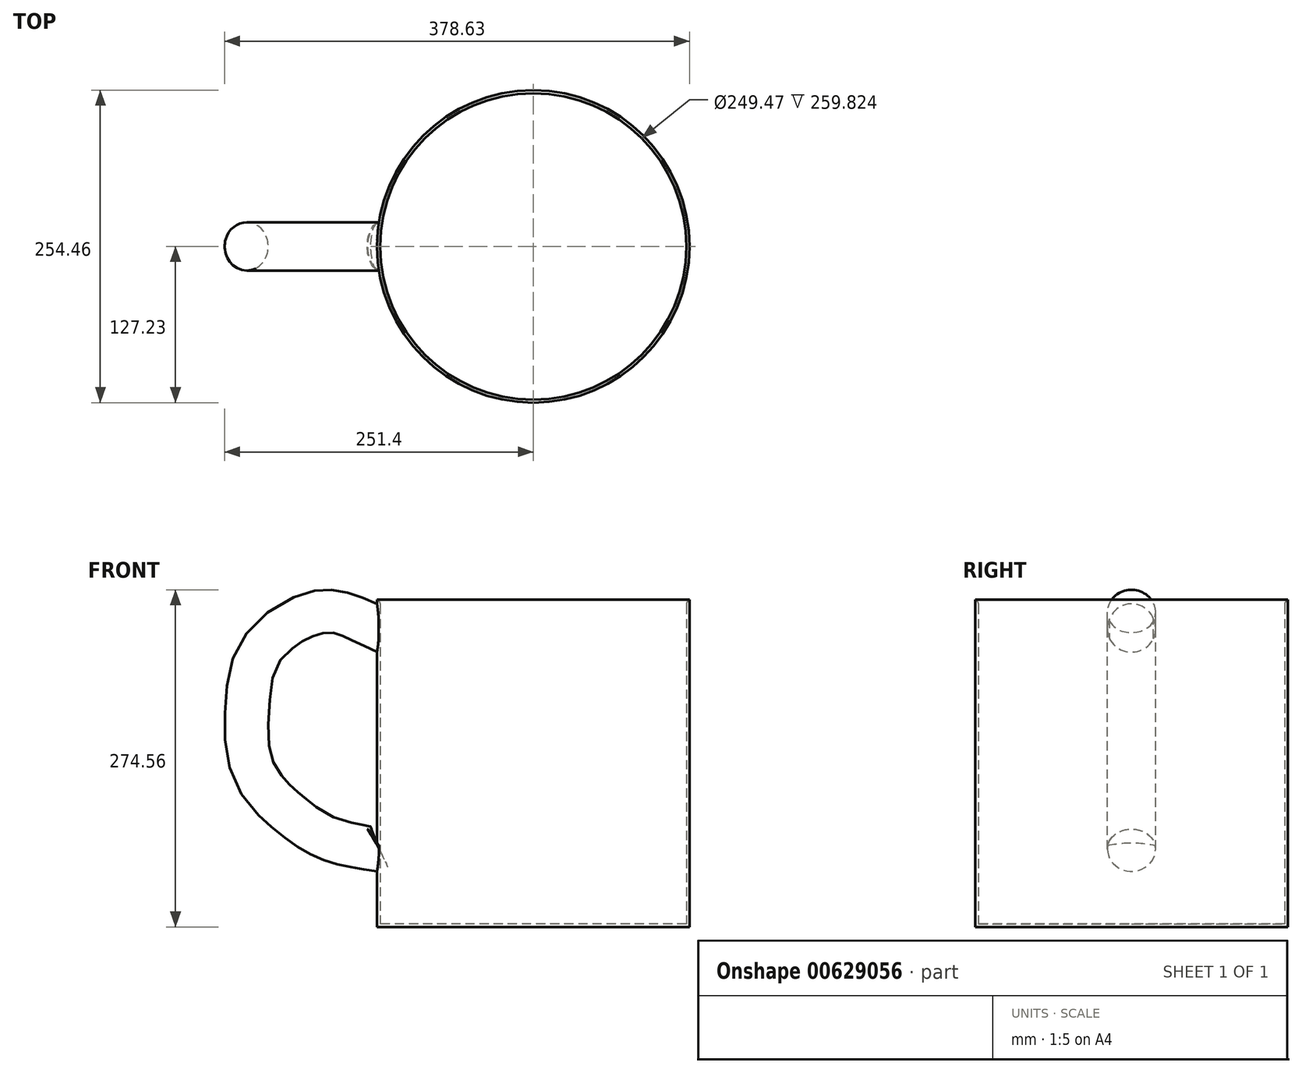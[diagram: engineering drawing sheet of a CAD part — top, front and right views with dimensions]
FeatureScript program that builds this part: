
annotation { "Feature Type Name" : "Feature", "Feature Type Description" : "" }
export const myFeature = defineFeature(function(context is Context, id is Id, definition is map)
    precondition{}
    {
        {
            var Q0;
            Q0=qCreatedBy(makeId("Top.planeOp"),FACE);
            var sketch = newSketch(context, id + "F0", { "sketchPlane" : qUnion([Q0])});
            skCircle(sketch, "E0", {"center": v(0, 0) * mm, "radius": 127.23 * mm});
            skSolve(sketch);
        }
        {
            var Q0;
            Q0 = qSketchRegion(id + "F0", true);
            extrude(context, id + "F1", {"entities" : qUnion([Q0]), "depth" : 266.7 * mm, "offsetDistance" : 25.4 * mm});
        }
        {
            var Q0;
            Q0=qCreatedBy(makeId("Front.planeOp"),FACE);
            var sketch = newSketch(context, id + "F2", { "sketchPlane" : qUnion([Q0])});
            skFitSpline(sketch, "E1", {"points": [v(-125.96, 244.42) * mm, v(-174.92, 257.06) * mm, v(-221.52, 227.05) * mm, v(-234.15, 180.45) * mm, v(-227.84, 125.17) * mm, v(-193.09, 86.48) * mm, v(-159.13, 68.31) * mm, v(-125.96, 62) * mm, v(-122.94, 62.13) * mm], "startDerivative": vector(-388.45, 179.87) * mm, "endDerivative": vector(138.8, 21.72) * mm});
            skSolve(sketch);
        }
        {
            var Q0;
            Q0=qCreatedBy(makeId("Right.planeOp"),FACE);
            cPlane(context, id + "F3", {"entities" : qUnion([Q0]), "cplaneType" : CPlaneType.OFFSET, "offset" : 128.27 * mm, "oppositeDirection" : true, "width" : 152.4 * mm, "height" : 152.4 * mm});
        }
        {
            var Q0;
            Q0=qCreatedBy(id+"F3.planeOp",FACE);
            var sketch = newSketch(context, id + "F4", { "sketchPlane" : qUnion([Q0])});
            skCircle(sketch, "E2", {"center": v(0, 244.04) * mm, "radius": 19.65 * mm});
            skSolve(sketch);
        }
        {
            var Q0;
            Q0 = qSketchRegion(id + "F4", true);
            var Q1;
            Q1 = qConstructionFilter(qBodyType(qCreatedBy(id + "F2" ,EDGE), BodyType.WIRE), ConstructionObject.NO);
            sweep(context, id + "F5", {"operationType" : NewBodyOperationType.ADD, "profiles" : qUnion([Q0]), "path" : qUnion([Q1])});
        }
        {
            var Q0;
            Q0=makeQuery(id+"F1.opExtrude","CAP_FACE",FACE,{"disambiguationData":[OSD([sQuery(id+"F0.wireOp",EDGE,"E0")])],"isStart":false});
            shell(context, id + "F6", {"entities" : qUnion([Q0]), "thickness" : 2.5 * mm});
        }
        {
            var Q0;
            {var subQ0=sQuery(id+"F0.wireOp",EDGE,"E0");Q0=makeQuery(id+"F6.opShell","OFFSET_EDGE",EDGE,{"disambiguationData":[OSD([subQ0]),TDD([makeQuery(id+"F1.opExtrude","CAP_EDGE",EDGE,{"disambiguationData":[OSD([subQ0])],"isStart":false})])]});}
            fillet(context, id + "F7", {"entities" : qUnion([Q0]), "radius" : 5.08 * mm, "tangentPropagation" : true, "allowEdgeOverflow" : false});
        }
    });
